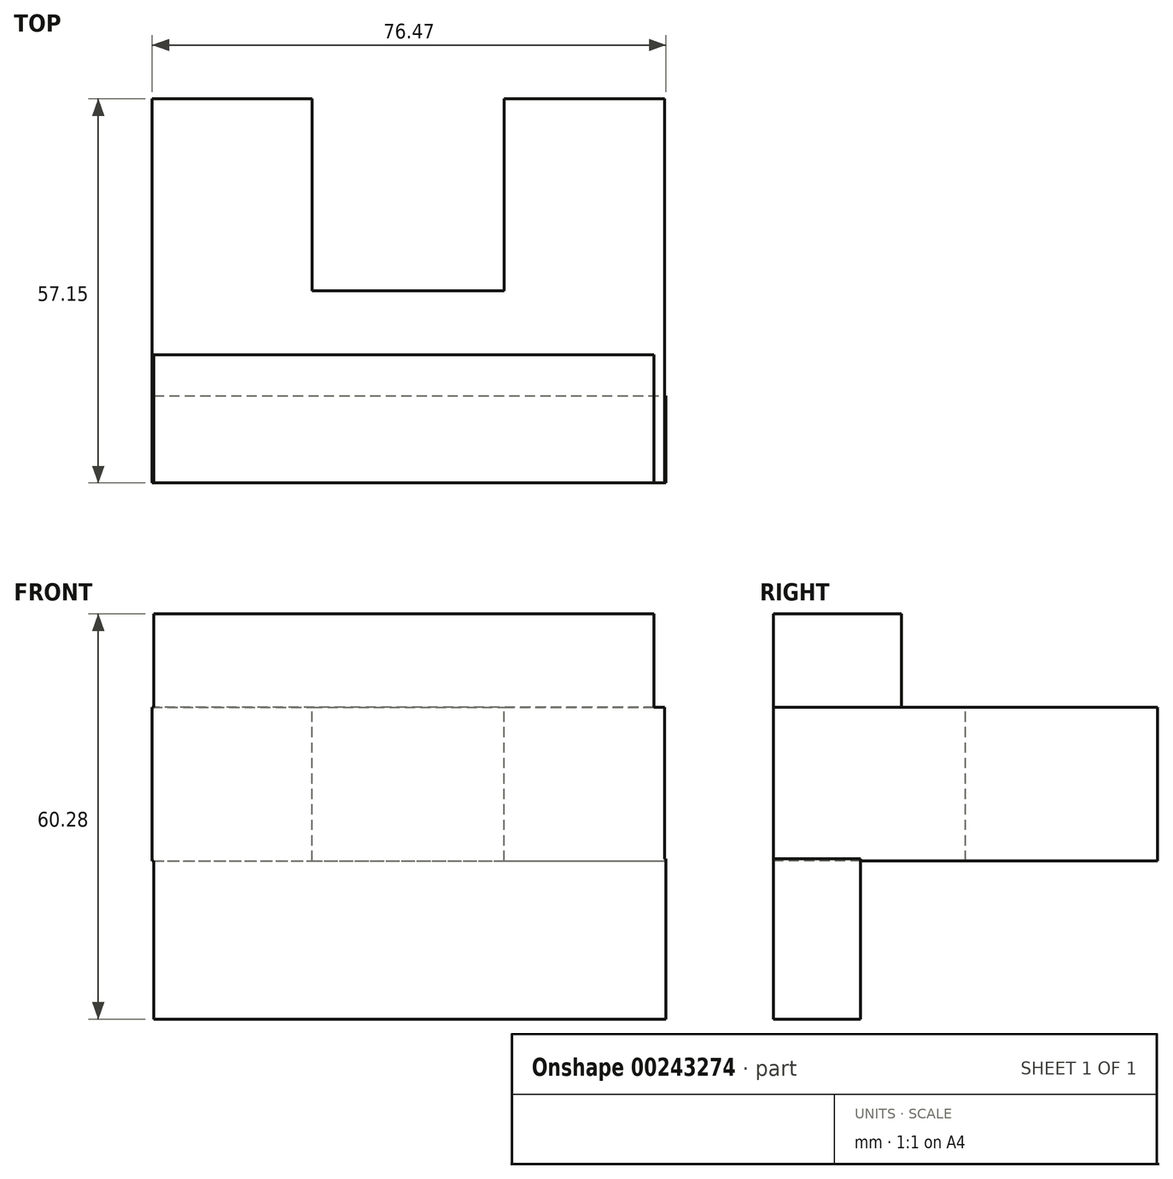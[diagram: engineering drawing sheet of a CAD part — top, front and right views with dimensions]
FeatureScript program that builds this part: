
annotation { "Feature Type Name" : "Feature", "Feature Type Description" : "" }
export const myFeature = defineFeature(function(context is Context, id is Id, definition is map)
    precondition{}
    {
        {
            var Q0;
            Q0=qCreatedBy(makeId("Front.planeOp"),FACE);
            var sketch = newSketch(context, id + "F0", { "sketchPlane" : qUnion([Q0])});
            skLineSegment(sketch, "E0", {"start": v(-46.94, -46.4) * mm, "end": v(29.26, -46.4) * mm});
            skLineSegment(sketch, "E1", {"start": v(29.26, -46.4) * mm, "end": v(29.26, -22.58) * mm});
            skLineSegment(sketch, "E2", {"start": v(29.26, -22.58) * mm, "end": v(-46.94, -22.58) * mm});
            skLineSegment(sketch, "E3", {"start": v(-46.94, -22.58) * mm, "end": v(-46.94, -46.4) * mm});
            skSolve(sketch);
        }
        {
            var Q0;
            Q0=qCreatedBy(makeId("Top.planeOp"),FACE);
            var sketch = newSketch(context, id + "F1", { "sketchPlane" : qUnion([Q0])});
            skLineSegment(sketch, "E4", {"start": v(-47.2, 0) * mm, "end": v(-47.2, 57.15) * mm});
            skLineSegment(sketch, "E5", {"start": v(-47.2, 57.15) * mm, "end": v(-23.38, 57.15) * mm});
            skLineSegment(sketch, "E6", {"start": v(-23.38, 57.15) * mm, "end": v(-23.38, 28.58) * mm});
            skLineSegment(sketch, "E7", {"start": v(-23.38, 28.58) * mm, "end": v(5.2, 28.58) * mm});
            skLineSegment(sketch, "E8", {"start": v(5.2, 28.58) * mm, "end": v(5.2, 57.15) * mm});
            skLineSegment(sketch, "E9", {"start": v(5.2, 57.15) * mm, "end": v(29.02, 57.15) * mm});
            skPoint(sketch, "E10.end.orphan", {"position": v(29.02, 0) * mm});
            skLineSegment(sketch, "E11", {"start": v(-47.2, 0) * mm, "end": v(29.02, 0) * mm});
            skLineSegment(sketch, "E12", {"start": v(29.02, 57.15) * mm, "end": v(29.02, 0) * mm});
            skSolve(sketch);
        }
        {
            var Q0;
            Q0=makeQuery(id+"F1.imprint","IMPRINT",FACE,{"disambiguationData":[TD([[makeQuery(id+"F1.imprint","IMPRINT",EDGE,{"derivedFrom":sQuery(id+"F1.wireOp",EDGE,"E4")}),-1.0]])]});
            extrude(context, id + "F2", {"entities" : qUnion([Q0]), "oppositeDirection" : true, "depth" : 22.86 * mm});
        }
        {
            var Q0;
            Q0 = qSketchRegion(id + "F0", true);
            extrude(context, id + "F3", {"entities" : qUnion([Q0]), "operationType" : NewBodyOperationType.ADD, "oppositeDirection" : true, "depth" : 12.95 * mm});
        }
        {
            var Q0;
            Q0=makeQuery(id+"F3.opExtrude","SWEPT_FACE",FACE,{"disambiguationData":[OSD([sQuery(id+"F0.wireOp",EDGE,"E3")])]});
            var sketch = newSketch(context, id + "F4", { "sketchPlane" : qUnion([Q0])});
            skLineSegment(sketch, "E13", {"start": v(0, 0) * mm, "end": v(0, 13.87) * mm});
            skLineSegment(sketch, "E14", {"start": v(0, 13.87) * mm, "end": v(-19.05, 13.87) * mm});
            skLineSegment(sketch, "E15", {"start": v(-19.05, 13.87) * mm, "end": v(-19.05, 0) * mm});
            skLineSegment(sketch, "E16", {"start": v(0, 13.87) * mm, "end": v(0, 0) * mm});
            skPoint(sketch, "E17.end.orphan", {"position": v(-56.54, -22.86) * mm});
            skLineSegment(sketch, "E18", {"start": v(-19.05, 0) * mm, "end": v(0, 0) * mm});
            skSolve(sketch);
        }
        {
            var Q0;
            Q0=makeQuery(id+"F4.imprint","IMPRINT",FACE,{"disambiguationData":[TD([[makeQuery(id+"F4.imprint","IMPRINT",EDGE,{"derivedFrom":sQuery(id+"F4.wireOp",EDGE,"E14")}),1.0]])]});
            extrude(context, id + "F5", {"entities" : qUnion([Q0]), "operationType" : NewBodyOperationType.ADD, "oppositeDirection" : true, "depth" : 74.42 * mm});
        }
    });
